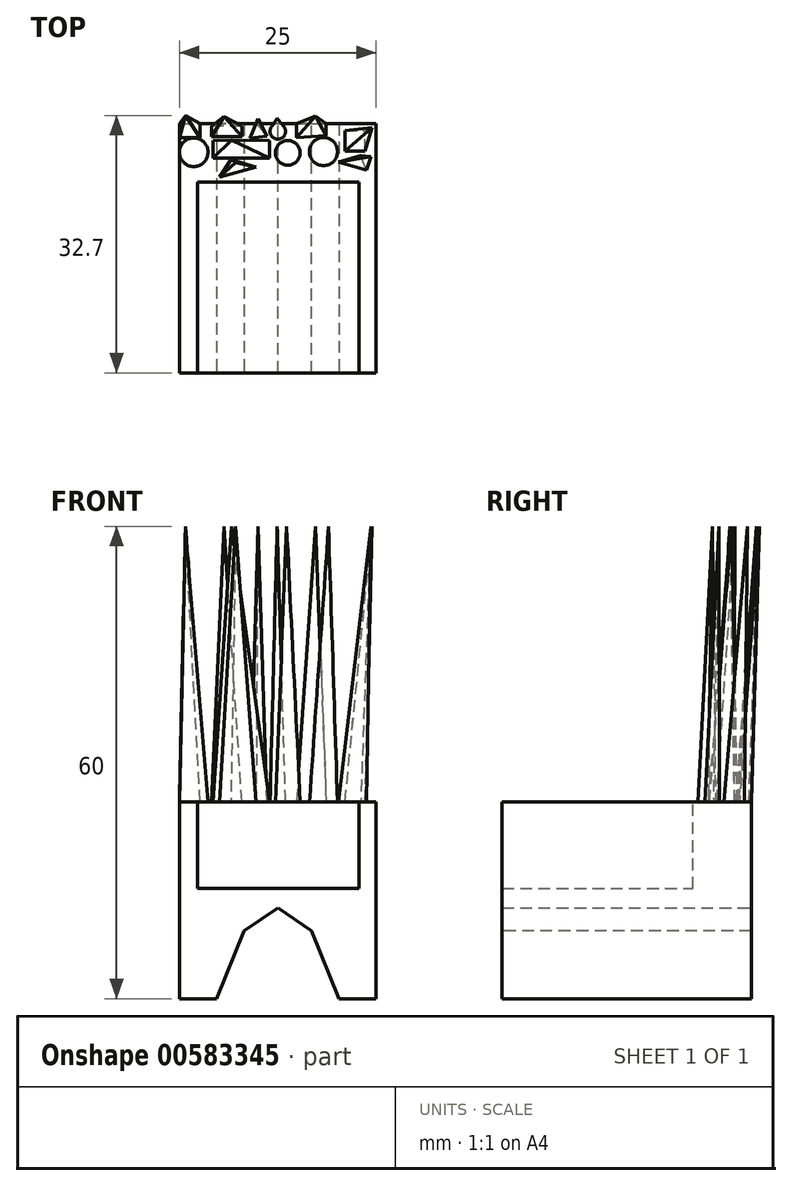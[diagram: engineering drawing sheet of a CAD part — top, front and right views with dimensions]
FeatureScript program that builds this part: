
annotation { "Feature Type Name" : "Feature", "Feature Type Description" : "" }
export const myFeature = defineFeature(function(context is Context, id is Id, definition is map)
    precondition{}
    {
        {
            var Q0;
            Q0=qCreatedBy(makeId("Top.planeOp"),FACE);
            var sketch = newSketch(context, id + "F0", { "sketchPlane" : qUnion([Q0])});
            skLineSegment(sketch, "E0.bottom", {"start": v(-12.5, -12.5) * mm, "end": v(12.5, -12.5) * mm});
            skLineSegment(sketch, "E0.top", {"start": v(-12.5, 12.5) * mm, "end": v(12.5, 12.5) * mm});
            skLineSegment(sketch, "E0.left", {"start": v(-12.5, -12.5) * mm, "end": v(-12.5, 12.5) * mm});
            skLineSegment(sketch, "E0.right", {"start": v(12.5, -12.5) * mm, "end": v(12.5, 12.5) * mm});
            skPoint(sketch, "E0.middle", {"position": v(0, 0) * mm});
            skLineSegment(sketch, "E1", {"start": v(-12.5, 12.5) * mm, "end": v(-12.5, 19.16) * mm});
            skLineSegment(sketch, "E2", {"start": v(-12.5, 19.16) * mm, "end": v(12.5, 19.16) * mm});
            skLineSegment(sketch, "E3", {"start": v(12.5, 19.16) * mm, "end": v(12.5, 12.5) * mm});
            skSolve(sketch);
        }
        {
            var Q0;
            Q0 = qSketchRegion(id + "F0", true);
            extrude(context, id + "F1", {"entities" : qUnion([Q0]), "depth" : 25 * mm, "offsetDistance" : 25 * mm});
        }
        {
            var Q0;
            Q0=makeQuery(id+"F1.opExtrude","SWEPT_FACE",FACE,{"disambiguationData":[OSD([sQuery(id+"F0.wireOp",EDGE,"E0.bottom")])]});
            var sketch = newSketch(context, id + "F2", { "sketchPlane" : qUnion([Q0])});
            skLineSegment(sketch, "E4", {"start": v(-7.79, 0) * mm, "end": v(-3.02, 11.76) * mm});
            skLineSegment(sketch, "E5", {"start": v(-7.3, 18.23) * mm, "end": v(7.3, 18.23) * mm});
            skLineSegment(sketch, "E6", {"start": v(0, 11.76) * mm, "end": v(0, 0) * mm});
            skLineSegment(sketch, "E7.MirrorCS", {"start": v(7.79, 0) * mm, "end": v(3.02, 11.76) * mm});
            skLineSegment(sketch, "E8", {"start": v(-3.02, 11.76) * mm, "end": v(3.02, 11.76) * mm});
            skPoint(sketch, "E9.orphan", {"position": v(-7.3, 18.23) * mm});
            skPoint(sketch, "E10.MirrorCS.start.orphan", {"position": v(0.4, 18.23) * mm});
            skPoint(sketch, "E11.orphan", {"position": v(-0.4, 18.23) * mm});
            skPoint(sketch, "E12.orphan", {"position": v(0, 18.23) * mm});
            skSolve(sketch);
        }
        {
            var Q0;
            {var subQ2=sQuery(id+"F2.wireOp",EDGE,"E6");Q0=makeQuery(id+"F2.imprint","IMPRINT",FACE,{"disambiguationData":[TD([[makeQuery(id+"F2.imprint","IMPRINT",EDGE,{"derivedFrom":subQ2}),1.0]])]});}
            var Q1;
            {var subQ2=sQuery(id+"F2.wireOp",EDGE,"E4");Q1=makeQuery(id+"F2.imprint","IMPRINT",FACE,{"disambiguationData":[TD([[makeQuery(id+"F2.imprint","IMPRINT",EDGE,{"derivedFrom":subQ2}),-1.0]])]});}
            extrude(context, id + "F3", {"entities" : qUnion([Q0, Q1]), "operationType" : NewBodyOperationType.REMOVE, "oppositeDirection" : true, "depth" : 35.6 * mm, "offsetDistance" : 25 * mm});
        }
        {
            var Q0;
            Q0=makeQuery(id+"F1.opExtrude","CAP_FACE",FACE,{"disambiguationData":[OSD([sQuery(id+"F0.wireOp",EDGE,"E0.bottom"),sQuery(id+"F0.wireOp",EDGE,"E0.top"),sQuery(id+"F0.wireOp",EDGE,"E0.left"),sQuery(id+"F0.wireOp",EDGE,"E0.right")])],"isStart":false});
            var sketch = newSketch(context, id + "F4", { "sketchPlane" : qUnion([Q0])});
            skLineSegment(sketch, "E13.bottom", {"start": v(-12.5, 19.16) * mm, "end": v(-9.89, 19.16) * mm});
            skLineSegment(sketch, "E13.top", {"start": v(-12.5, 17.36) * mm, "end": v(-9.89, 17.36) * mm});
            skLineSegment(sketch, "E13.left", {"start": v(-12.5, 19.16) * mm, "end": v(-12.5, 17.36) * mm});
            skLineSegment(sketch, "E13.right", {"start": v(-9.89, 19.16) * mm, "end": v(-9.89, 17.36) * mm});
            skPoint(sketch, "E13.middle", {"position": v(-11.2, 18.26) * mm});
            skLineSegment(sketch, "E14.bottom", {"start": v(-8.2, 16.98) * mm, "end": v(-1.03, 16.98) * mm});
            skLineSegment(sketch, "E14.top", {"start": v(-8.2, 14.76) * mm, "end": v(-1.03, 14.76) * mm});
            skLineSegment(sketch, "E14.left", {"start": v(-8.2, 16.98) * mm, "end": v(-8.2, 14.76) * mm});
            skLineSegment(sketch, "E14.right", {"start": v(-1.03, 16.98) * mm, "end": v(-1.03, 14.76) * mm});
            skPoint(sketch, "E14.middle", {"position": v(-4.62, 15.87) * mm});
            skLineSegment(sketch, "E15.bottom", {"start": v(6.14, 19.16) * mm, "end": v(2.39, 19.16) * mm});
            skLineSegment(sketch, "E15.left", {"start": v(6.14, 19.16) * mm, "end": v(6.14, 17.65) * mm});
            skLineSegment(sketch, "E15.right", {"start": v(2.39, 19.16) * mm, "end": v(2.39, 17.36) * mm});
            skPoint(sketch, "E15.middle", {"position": v(4.27, 18.26) * mm});
            skLineSegment(sketch, "E16.bottom", {"start": v(8.54, 15.7) * mm, "end": v(11.1, 15.7) * mm});
            skLineSegment(sketch, "E16.top", {"start": v(8.54, 18.26) * mm, "end": v(11.1, 18.26) * mm});
            skLineSegment(sketch, "E16.left", {"start": v(8.54, 15.7) * mm, "end": v(8.54, 18.26) * mm});
            skLineSegment(sketch, "E16.right", {"start": v(11.1, 15.7) * mm, "end": v(11.1, 18.26) * mm});
            skPoint(sketch, "E16.middle", {"position": v(9.82, 16.98) * mm});
            skCircle(sketch, "E17", {"center": v(0, 18.17) * mm, "radius": 0.99 * mm});
            skCircle(sketch, "E18", {"center": v(-10.68, 15.52) * mm, "radius": 1.82 * mm});
            skCircle(sketch, "E19", {"center": v(5.8, 15.61) * mm, "radius": 1.78 * mm});
            skCircle(sketch, "E20", {"center": v(1.28, 15.44) * mm, "radius": 1.57 * mm});
            skLineSegment(sketch, "E21.bottom", {"start": v(-4.56, 17.53) * mm, "end": v(-8.43, 17.53) * mm});
            skLineSegment(sketch, "E21.top", {"start": v(-4.56, 18.86) * mm, "end": v(-8.43, 18.86) * mm});
            skLineSegment(sketch, "E21.left", {"start": v(-4.56, 17.53) * mm, "end": v(-4.56, 18.86) * mm});
            skLineSegment(sketch, "E21.right", {"start": v(-8.43, 17.53) * mm, "end": v(-8.43, 18.86) * mm});
            skPoint(sketch, "E21.middle", {"position": v(-6.5, 18.2) * mm});
            skLineSegment(sketch, "E22", {"start": v(-2.7, 19.16) * mm, "end": v(-1.36, 17.6) * mm});
            skLineSegment(sketch, "E23", {"start": v(-1.36, 17.6) * mm, "end": v(-3.51, 17.3) * mm});
            skLineSegment(sketch, "E24", {"start": v(-3.51, 17.3) * mm, "end": v(-2.7, 19.16) * mm});
            skLineSegment(sketch, "E25", {"start": v(10.53, 15.12) * mm, "end": v(7.7, 14.3) * mm});
            skLineSegment(sketch, "E26", {"start": v(7.7, 14.3) * mm, "end": v(11.25, 13.28) * mm});
            skLineSegment(sketch, "E27", {"start": v(11.25, 13.28) * mm, "end": v(10.53, 15.12) * mm});
            skLineSegment(sketch, "E28", {"start": v(-7.39, 12.34) * mm, "end": v(-5.96, 14.58) * mm});
            skLineSegment(sketch, "E29", {"start": v(-5.96, 14.58) * mm, "end": v(-2.75, 13.66) * mm});
            skLineSegment(sketch, "E30", {"start": v(-2.75, 13.66) * mm, "end": v(-7.39, 12.34) * mm});
            skLineSegment(sketch, "E31", {"start": v(2.39, 17.36) * mm, "end": v(6.14, 17.65) * mm});
            skSolve(sketch);
        }
        {
            var Q0;
            {var subQ8=sQuery(id+"F4.wireOp",EDGE,"E13.top");Q0=makeQuery(id+"F4.imprint","IMPRINT",FACE,{"disambiguationData":[TD([[makeQuery(id+"F4.imprint","IMPRINT",EDGE,{"derivedFrom":subQ8}),-1.0]])]});}
            cPlane(context, id + "F5", {"entities" : qUnion([Q0]), "cplaneType" : CPlaneType.OFFSET, "offset" : 35 * mm, "width" : 150 * mm, "height" : 150 * mm});
        }
        {
            var Q0;
            Q0=qCreatedBy(id+"F5.planeOp",FACE);
            var sketch = newSketch(context, id + "F6", { "sketchPlane" : qUnion([Q0])});
            skPoint(sketch, "E32", {"position": v(-11.74, 20.2) * mm});
            skPoint(sketch, "E33", {"position": v(-6.85, 20.08) * mm});
            skPoint(sketch, "E34", {"position": v(-2.5, 19.78) * mm});
            skPoint(sketch, "E35", {"position": v(-0.09, 19.84) * mm});
            skPoint(sketch, "E36", {"position": v(4.8, 20.14) * mm});
            skPoint(sketch, "E37", {"position": v(12, 18.63) * mm});
            skPoint(sketch, "E38", {"position": v(11.8, 15) * mm});
            skPoint(sketch, "E39", {"position": v(6.43, 16.64) * mm});
            skPoint(sketch, "E40", {"position": v(1.12, 16.45) * mm});
            skPoint(sketch, "E41", {"position": v(-5.89, 17.06) * mm});
            skPoint(sketch, "E42", {"position": v(-11.74, 16.82) * mm});
            skPoint(sketch, "E43", {"position": v(-5.34, 14.22) * mm});
            skSolve(sketch);
        }
        {
            var Q1;
            Q1=makeQuery(id+"F4.imprint","IMPRINT",FACE,{"disambiguationData":[TD([[makeQuery(id+"F4.imprint","IMPRINT",EDGE,{"derivedFrom":sQuery(id+"F4.wireOp",EDGE,"E18")}),1.0]])]});
            var Q2;
            Q2=sQuery(id+"F6.wireOp",VERTEX,"E42");
            loft(context, id + "F7", {"operationType" : NewBodyOperationType.ADD, "sheetProfilesArray" : [{ "sheetProfileEntities" : qUnion([Q1]) }, { "sheetProfileEntities" : qUnion([Q2]) }]});
        }
        {
            var Q1;
            Q1=makeQuery(id+"F4.imprint","IMPRINT",FACE,{"disambiguationData":[TD([[makeQuery(id+"F4.imprint","IMPRINT",EDGE,{"derivedFrom":sQuery(id+"F4.wireOp",EDGE,"E13.bottom")}),-1.0]])]});
            var Q2;
            Q2=sQuery(id+"F6.wireOp",VERTEX,"E32");
            loft(context, id + "F8", {"operationType" : NewBodyOperationType.ADD, "sheetProfilesArray" : [{ "sheetProfileEntities" : qUnion([Q1]) }, { "sheetProfileEntities" : qUnion([Q2]) }]});
        }
        {
            var Q1;
            Q1=sQuery(id+"F6.wireOp",VERTEX,"E38");
            var Q2;
            Q2=makeQuery(id+"F4.imprint","IMPRINT",FACE,{"disambiguationData":[TD([[makeQuery(id+"F4.imprint","IMPRINT",EDGE,{"derivedFrom":sQuery(id+"F4.wireOp",EDGE,"E25")}),1.0]])]});
            loft(context, id + "F9", {"operationType" : NewBodyOperationType.ADD, "sheetProfilesArray" : [{ "sheetProfileEntities" : qUnion([Q1]) }, { "sheetProfileEntities" : qUnion([Q2]) }]});
        }
        {
            var Q1;
            Q1=makeQuery(id+"F4.imprint","IMPRINT",FACE,{"disambiguationData":[TD([[makeQuery(id+"F4.imprint","IMPRINT",EDGE,{"derivedFrom":sQuery(id+"F4.wireOp",EDGE,"E14.bottom")}),-1.0]])]});
            var Q2;
            Q2=sQuery(id+"F6.wireOp",VERTEX,"E41");
            loft(context, id + "F10", {"operationType" : NewBodyOperationType.ADD, "sheetProfilesArray" : [{ "sheetProfileEntities" : qUnion([Q1]) }, { "sheetProfileEntities" : qUnion([Q2]) }]});
        }
        {
            var Q1;
            Q1=sQuery(id+"F6.wireOp",VERTEX,"E43");
            var Q2;
            Q2=makeQuery(id+"F4.imprint","IMPRINT",FACE,{"disambiguationData":[TD([[makeQuery(id+"F4.imprint","IMPRINT",EDGE,{"derivedFrom":sQuery(id+"F4.wireOp",EDGE,"E28")}),-1.0]])]});
            loft(context, id + "F11", {"operationType" : NewBodyOperationType.ADD, "sheetProfilesArray" : [{ "sheetProfileEntities" : qUnion([Q1]) }, { "sheetProfileEntities" : qUnion([Q2]) }]});
        }
        {
            var Q1;
            Q1=makeQuery(id+"F4.imprint","IMPRINT",FACE,{"disambiguationData":[TD([[makeQuery(id+"F4.imprint","IMPRINT",EDGE,{"derivedFrom":sQuery(id+"F4.wireOp",EDGE,"E21.bottom")}),-1.0]])]});
            var Q2;
            Q2=sQuery(id+"F6.wireOp",VERTEX,"E33");
            loft(context, id + "F12", {"operationType" : NewBodyOperationType.ADD, "sheetProfilesArray" : [{ "sheetProfileEntities" : qUnion([Q1]) }, { "sheetProfileEntities" : qUnion([Q2]) }]});
        }
        {
            var Q1;
            Q1=makeQuery(id+"F4.imprint","IMPRINT",FACE,{"disambiguationData":[TD([[makeQuery(id+"F4.imprint","IMPRINT",EDGE,{"derivedFrom":sQuery(id+"F4.wireOp",EDGE,"E22")}),-1.0]])]});
            var Q2;
            Q2=sQuery(id+"F6.wireOp",VERTEX,"E34");
            loft(context, id + "F13", {"operationType" : NewBodyOperationType.ADD, "sheetProfilesArray" : [{ "sheetProfileEntities" : qUnion([Q1]) }, { "sheetProfileEntities" : qUnion([Q2]) }]});
        }
        {
            var Q1;
            Q1=sQuery(id+"F6.wireOp",VERTEX,"E40");
            var Q2;
            Q2=makeQuery(id+"F4.imprint","IMPRINT",FACE,{"disambiguationData":[TD([[makeQuery(id+"F4.imprint","IMPRINT",EDGE,{"derivedFrom":sQuery(id+"F4.wireOp",EDGE,"E20")}),1.0]])]});
            loft(context, id + "F14", {"operationType" : NewBodyOperationType.ADD, "sheetProfilesArray" : [{ "sheetProfileEntities" : qUnion([Q1]) }, { "sheetProfileEntities" : qUnion([Q2]) }]});
        }
        {
            var Q1;
            Q1=sQuery(id+"F6.wireOp",VERTEX,"E35");
            var Q2;
            Q2=makeQuery(id+"F4.imprint","IMPRINT",FACE,{"disambiguationData":[TD([[makeQuery(id+"F4.imprint","IMPRINT",EDGE,{"derivedFrom":sQuery(id+"F4.wireOp",EDGE,"E17")}),1.0]])]});
            loft(context, id + "F15", {"operationType" : NewBodyOperationType.ADD, "sheetProfilesArray" : [{ "sheetProfileEntities" : qUnion([Q1]) }, { "sheetProfileEntities" : qUnion([Q2]) }]});
        }
        {
            var Q1;
            Q1=sQuery(id+"F6.wireOp",VERTEX,"E36");
            var Q2;
            Q2=makeQuery(id+"F4.imprint","IMPRINT",FACE,{"disambiguationData":[TD([[makeQuery(id+"F4.imprint","IMPRINT",EDGE,{"derivedFrom":sQuery(id+"F4.wireOp",EDGE,"E15.bottom")}),-1.0]])]});
            loft(context, id + "F16", {"operationType" : NewBodyOperationType.ADD, "sheetProfilesArray" : [{ "sheetProfileEntities" : qUnion([Q1]) }, { "sheetProfileEntities" : qUnion([Q2]) }]});
        }
        {
            var Q1;
            Q1=sQuery(id+"F6.wireOp",VERTEX,"E39");
            var Q2;
            Q2=makeQuery(id+"F4.imprint","IMPRINT",FACE,{"disambiguationData":[TD([[makeQuery(id+"F4.imprint","IMPRINT",EDGE,{"derivedFrom":sQuery(id+"F4.wireOp",EDGE,"E19")}),1.0]])]});
            loft(context, id + "F17", {"operationType" : NewBodyOperationType.ADD, "sheetProfilesArray" : [{ "sheetProfileEntities" : qUnion([Q1]) }, { "sheetProfileEntities" : qUnion([Q2]) }]});
        }
        {
            var Q1;
            Q1=makeQuery(id+"F4.imprint","IMPRINT",FACE,{"disambiguationData":[TD([[makeQuery(id+"F4.imprint","IMPRINT",EDGE,{"derivedFrom":sQuery(id+"F4.wireOp",EDGE,"E16.bottom")}),1.0]])]});
            var Q2;
            Q2=sQuery(id+"F6.wireOp",VERTEX,"E37");
            loft(context, id + "F18", {"operationType" : NewBodyOperationType.ADD, "sheetProfilesArray" : [{ "sheetProfileEntities" : qUnion([Q1]) }, { "sheetProfileEntities" : qUnion([Q2]) }]});
        }
        {
            var Q0;
            {var subQ8=sQuery(id+"F4.wireOp",EDGE,"E13.top");Q0=makeQuery(id+"F4.imprint","IMPRINT",FACE,{"disambiguationData":[TD([[makeQuery(id+"F4.imprint","IMPRINT",EDGE,{"derivedFrom":subQ8}),-1.0]])]});}
            var sketch = newSketch(context, id + "F19", { "sketchPlane" : qUnion([Q0])});
            skLineSegment(sketch, "E44.0", {"start": v(12.43, -12.5) * mm, "end": v(12.43, 12.5) * mm});
            skLineSegment(sketch, "E45", {"start": v(10.3, -12.43) * mm, "end": v(10.3, 11.75) * mm});
            skLineSegment(sketch, "E46", {"start": v(10.3, 11.75) * mm, "end": v(-10.22, 11.75) * mm});
            skLineSegment(sketch, "E47", {"start": v(-10.22, 11.75) * mm, "end": v(-10.22, -12.33) * mm});
            skLineSegment(sketch, "E48", {"start": v(-10.22, -12.33) * mm, "end": v(-10.22, -14.36) * mm});
            skLineSegment(sketch, "E49", {"start": v(-10.22, -14.36) * mm, "end": v(10.3, -14.36) * mm});
            skLineSegment(sketch, "E50", {"start": v(10.3, -14.36) * mm, "end": v(10.3, -12.43) * mm});
            skSolve(sketch);
        }
        {
            var Q0;
            Q0 = qSketchRegion(id + "F19", true);
            extrude(context, id + "F20", {"entities" : qUnion([Q0]), "operationType" : NewBodyOperationType.REMOVE, "oppositeDirection" : true, "depth" : 11 * mm, "offsetDistance" : 25 * mm});
        }
        {
            var Q0;
            Q0=makeQuery(id+"F3.boolean.opBoolean","COPY",EDGE,{"derivedFrom":makeQuery(id+"F3.opExtrude","SWEPT_EDGE",EDGE,{"disambiguationData":[OSD([sQuery(id+"F2.wireOp",EDGE,"E4"),sQuery(id+"F2.wireOp",EDGE,"E8")])]})});
            var Q1;
            Q1=makeQuery(id+"F3.boolean.opBoolean","COPY",EDGE,{"derivedFrom":makeQuery(id+"F3.opExtrude","SWEPT_EDGE",EDGE,{"disambiguationData":[OSD([sQuery(id+"F2.wireOp",EDGE,"E7.MirrorCS"),sQuery(id+"F2.wireOp",EDGE,"E8")])]})});
            chamfer(context, id + "F21", {"entities" : qUnion([Q0, Q1]), "width" : 5 * mm, "tangentPropagation" : true});
        }
    });
